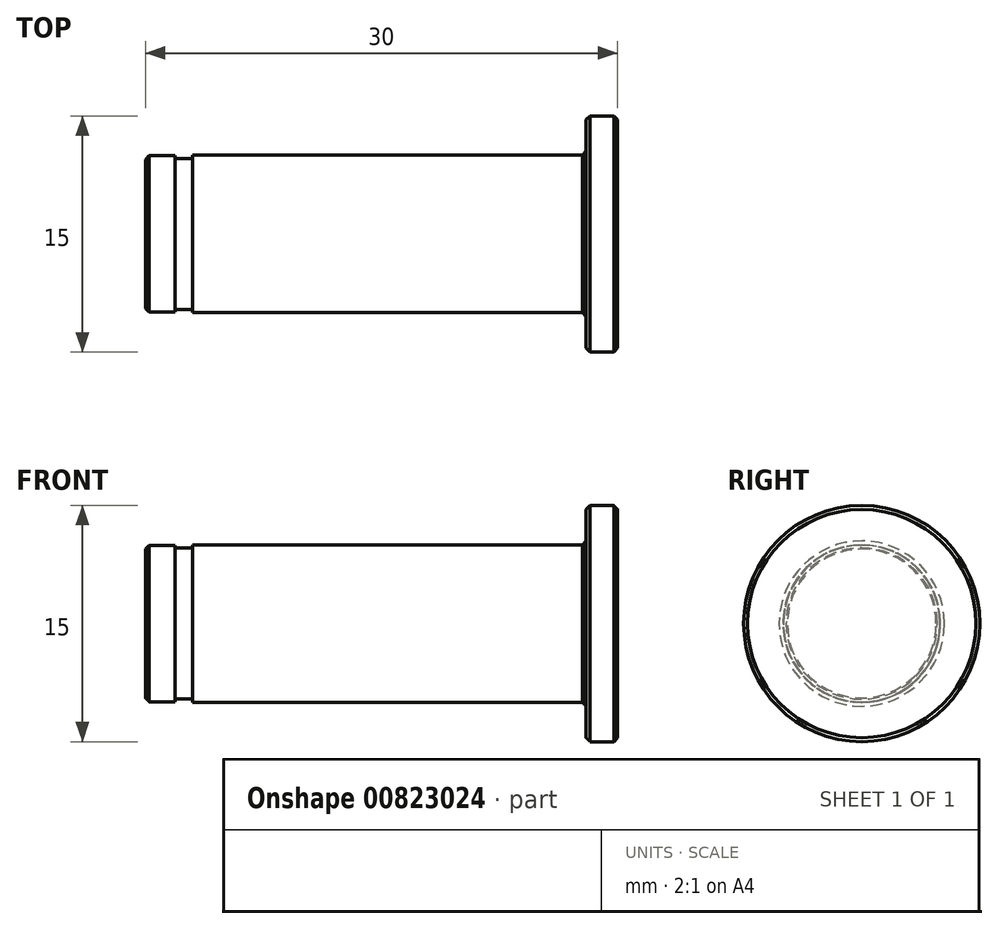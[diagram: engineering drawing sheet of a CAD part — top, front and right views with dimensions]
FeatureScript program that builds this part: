
annotation { "Feature Type Name" : "Feature", "Feature Type Description" : "" }
export const myFeature = defineFeature(function(context is Context, id is Id, definition is map)
    precondition{}
    {
        {
            var Q0;
            Q0=qCreatedBy(makeId("Front.planeOp"),FACE);
            var sketch = newSketch(context, id + "F0", { "sketchPlane" : qUnion([Q0])});
            skLineSegment(sketch, "E0", {"start": v(0, 0) * mm, "end": v(5.59, 0) * mm, "construction": true});
            skLineSegment(sketch, "E1", {"start": v(0, 0) * mm, "end": v(0, 7.5) * mm});
            skLineSegment(sketch, "E2", {"start": v(0, 7.5) * mm, "end": v(-2, 7.5) * mm});
            skLineSegment(sketch, "E3", {"start": v(-2, 7.5) * mm, "end": v(-2, 5) * mm});
            skLineSegment(sketch, "E4", {"start": v(-2, 5) * mm, "end": v(-27, 5) * mm});
            skLineSegment(sketch, "E5", {"start": v(-27, 5) * mm, "end": v(-27, 4.8) * mm});
            skLineSegment(sketch, "E6", {"start": v(-27, 4.8) * mm, "end": v(-28.1, 4.8) * mm});
            skLineSegment(sketch, "E7", {"start": v(-28.1, 4.8) * mm, "end": v(-28.1, 4.97) * mm});
            skLineSegment(sketch, "E8", {"start": v(-28.1, 4.97) * mm, "end": v(-30, 4.97) * mm});
            skLineSegment(sketch, "E9", {"start": v(-30, 4.97) * mm, "end": v(-30, 0) * mm});
            skLineSegment(sketch, "E10", {"start": v(-30, 0) * mm, "end": v(0, 0) * mm});
            skSolve(sketch);
        }
        {
            var Q0;
            Q0=makeQuery(id+"F0.imprint","IMPRINT",FACE,{"disambiguationData":[TD([[makeQuery(id+"F0.imprint","IMPRINT",EDGE,{"derivedFrom":sQuery(id+"F0.wireOp",EDGE,"E1")}),1.0]])]});
            var Q1;
            Q1=sQuery(id+"F0.wireOp",EDGE,"E0");
            revolve(context, id + "F1", {"surfaceOperationType" : NewSurfaceOperationType.NEW, "entities" : qUnion([Q0]), "axis" : qUnion([Q1]), "revolveType" : RevolveType.FULL});
        }
        {
            var Q0;
            Q0=makeQuery(id+"F1.opRevolve","SWEPT_FACE",FACE,{"disambiguationData":[OSD([sQuery(id+"F0.wireOp",EDGE,"E3")])]});
            var Q1;
            Q1=makeQuery(id+"F1.opRevolve","SWEPT_FACE",FACE,{"disambiguationData":[OSD([sQuery(id+"F0.wireOp",EDGE,"E1")])]});
            var Q2;
            Q2=makeQuery(id+"F1.opRevolve","SWEPT_FACE",FACE,{"disambiguationData":[OSD([sQuery(id+"F0.wireOp",EDGE,"E9")])]});
            chamfer(context, id + "F2", {"entities" : qUnion([Q0, Q1, Q2]), "width" : 0.25 * mm, "tangentPropagation" : true});
        }
    });
